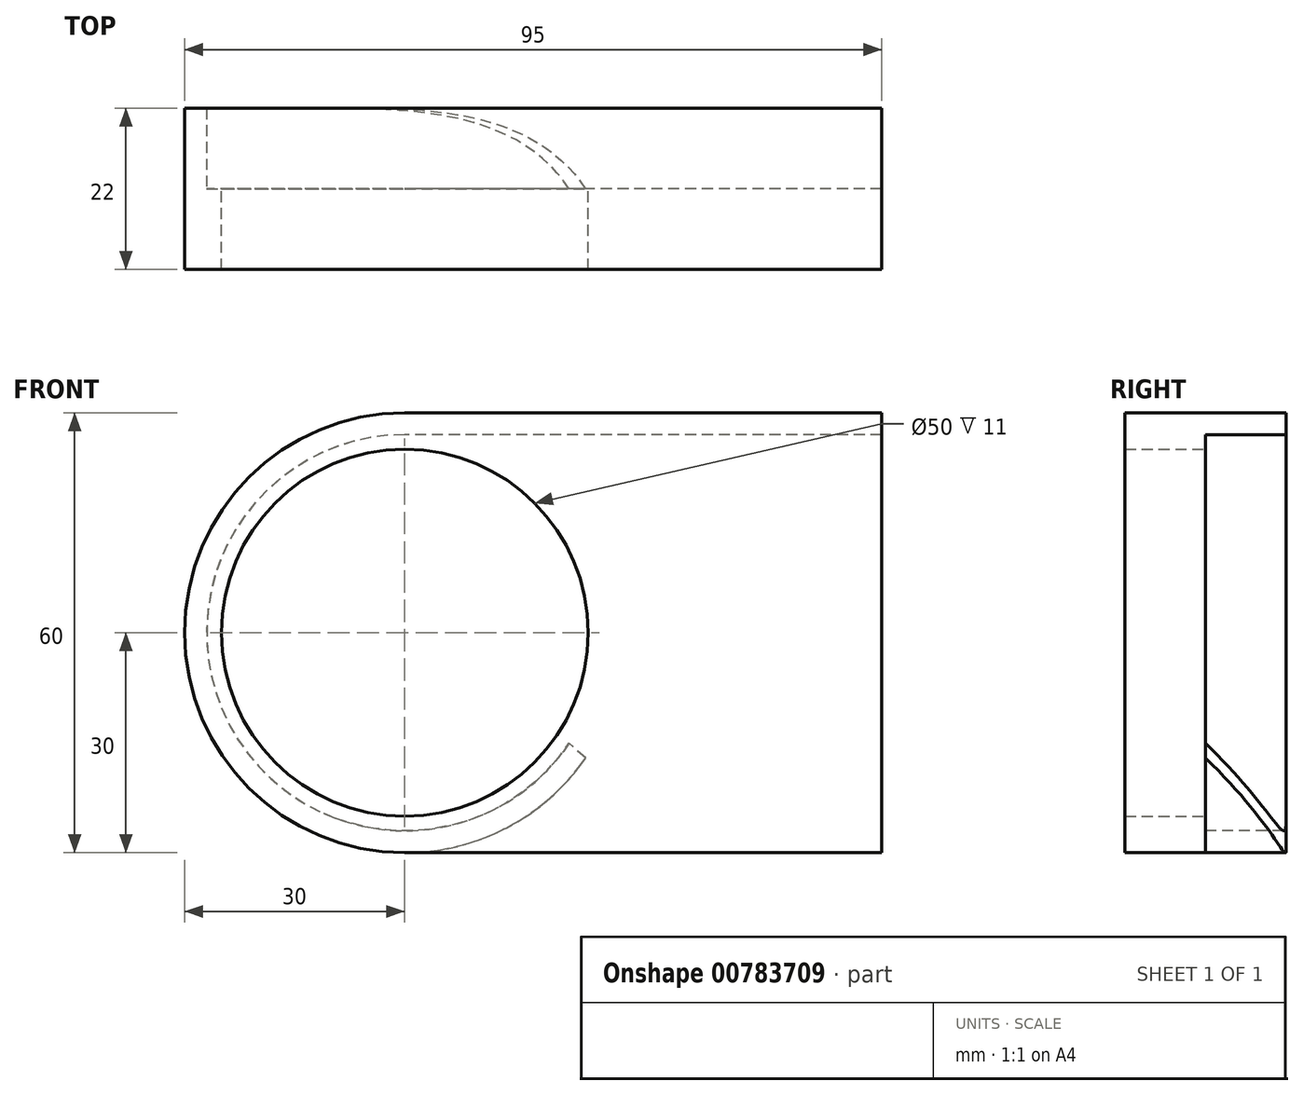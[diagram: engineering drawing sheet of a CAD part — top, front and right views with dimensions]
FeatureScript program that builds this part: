
annotation { "Feature Type Name" : "Feature", "Feature Type Description" : "" }
export const myFeature = defineFeature(function(context is Context, id is Id, definition is map)
    precondition{}
    {
        {
            var Q0;
            Q0=qCreatedBy(makeId("Front.planeOp"),FACE);
            var sketch = newSketch(context, id + "F0", { "sketchPlane" : qUnion([Q0])});
            skLineSegment(sketch, "E0.bottom", {"start": v(47.5, -30) * mm, "end": v(-17.5, -30) * mm});
            skLineSegment(sketch, "E0.top", {"start": v(47.5, 30) * mm, "end": v(-17.5, 30) * mm});
            skLineSegment(sketch, "E0.left", {"start": v(47.5, -30) * mm, "end": v(47.5, 30) * mm});
            skPoint(sketch, "E0.middle", {"position": v(0, 0) * mm});
            skCircle(sketch, "E1", {"center": v(-17.5, 0) * mm, "radius": 30 * mm});
            skPoint(sketch, "E1.first.point", {"position": v(-47.5, 0) * mm});
            skPoint(sketch, "E1.second.point", {"position": v(12.5, 0) * mm});
            skPoint(sketch, "E1.third.point", {"position": v(-17.5, -30) * mm});
            skPoint(sketch, "E2.orphan", {"position": v(-47.5, 30) * mm});
            skPoint(sketch, "E3.orphan", {"position": v(-47.5, -30) * mm});
            skCircle(sketch, "E4.0", {"center": v(-17.5, 0) * mm, "radius": 25 * mm});
            skSolve(sketch);
        }
        {
            var Q0;
            Q0 = qSketchRegion(id + "F0", true);
            extrude(context, id + "F1", {"entities" : qUnion([Q0]), "depth" : 11 * mm, "offsetDistance" : 25 * mm});
        }
        {
            var Q0;
            Q0=makeQuery(id+"F1.opExtrude","CAP_FACE",FACE,{"disambiguationData":[OSD([sQuery(id+"F0.wireOp",EDGE,"E0.bottom"),sQuery(id+"F0.wireOp",EDGE,"E0.top"),sQuery(id+"F0.wireOp",EDGE,"E0.left"),sQuery(id+"F0.wireOp",EDGE,"E1"),sQuery(id+"F0.wireOp",EDGE,"E4.0")])],"isStart":true});
            var sketch = newSketch(context, id + "F2", { "sketchPlane" : qUnion([Q0])});
            skArc(sketch, "E5", {"start": v(17.5, -30) * mm, "mid": v(47.5, 0) * mm, "end": v(17.5, 30) * mm});
            skPoint(sketch, "E5.first.point", {"position": v(47.5, 0) * mm});
            skPoint(sketch, "E5.second.point", {"position": v(17.5, -30) * mm});
            skPoint(sketch, "E5.third.point", {"position": v(17.5, 30) * mm});
            skLineSegment(sketch, "E6.bottom", {"start": v(-47.5, 30) * mm, "end": v(17.51, 30) * mm});
            skLineSegment(sketch, "E6.top", {"start": v(-47.5, 27) * mm, "end": v(4.42, 27) * mm});
            skLineSegment(sketch, "E6.left", {"start": v(-47.5, 30) * mm, "end": v(-47.5, 27) * mm});
            skArc(sketch, "E7.0", {"start": v(-4.9, -15.08) * mm, "mid": v(41.34, -12.68) * mm, "end": v(17.5, 27) * mm});
            skLineSegment(sketch, "E8.trimOffspring", {"start": v(17.5, 27) * mm, "end": v(17.51, 27) * mm});
            skPoint(sketch, "E9.endSnap0", {"position": v(-15, -30) * mm});
            skLineSegment(sketch, "E10", {"start": v(4.42, 27) * mm, "end": v(17.51, 27) * mm});
            skArc(sketch, "E11", {"start": v(4.42, -27) * mm, "mid": v(10.8, -29.24) * mm, "end": v(17.5, -30) * mm});
            skPoint(sketch, "E9.end.orphan", {"position": v(-12.5, -30) * mm});
            skArc(sketch, "E12.trimOffspring", {"start": v(-7.14, -17.1) * mm, "mid": v(-2, -22.8) * mm, "end": v(4.42, -27) * mm});
            skLineSegment(sketch, "E13", {"start": v(-7.14, -17.1) * mm, "end": v(-4.9, -15.08) * mm});
            skSolve(sketch);
        }
        {
            var Q0;
            {var subQ5=sQuery(id+"F2.wireOp",EDGE,"E5");Q0=makeQuery(id+"F2.imprint","IMPRINT",FACE,{"disambiguationData":[TD([[makeQuery(id+"F2.imprint","IMPRINT",EDGE,{"derivedFrom":subQ5}),-1.0]])]});}
            extrude(context, id + "F3", {"entities" : qUnion([Q0]), "operationType" : NewBodyOperationType.ADD, "depth" : 11 * mm, "offsetDistance" : 25 * mm});
        }
        {
            var Q0;
            Q0=makeQuery(id+"F3.opExtrude","CAP_EDGE",EDGE,{"disambiguationData":[OSD([sQuery(id+"F2.wireOp",EDGE,"E13")])],"isStart":false});
            fillet(context, id + "F4", {"entities" : qUnion([Q0]), "radius" : 45 * mm, "tangentPropagation" : true, "allowEdgeOverflow" : false});
        }
    });
